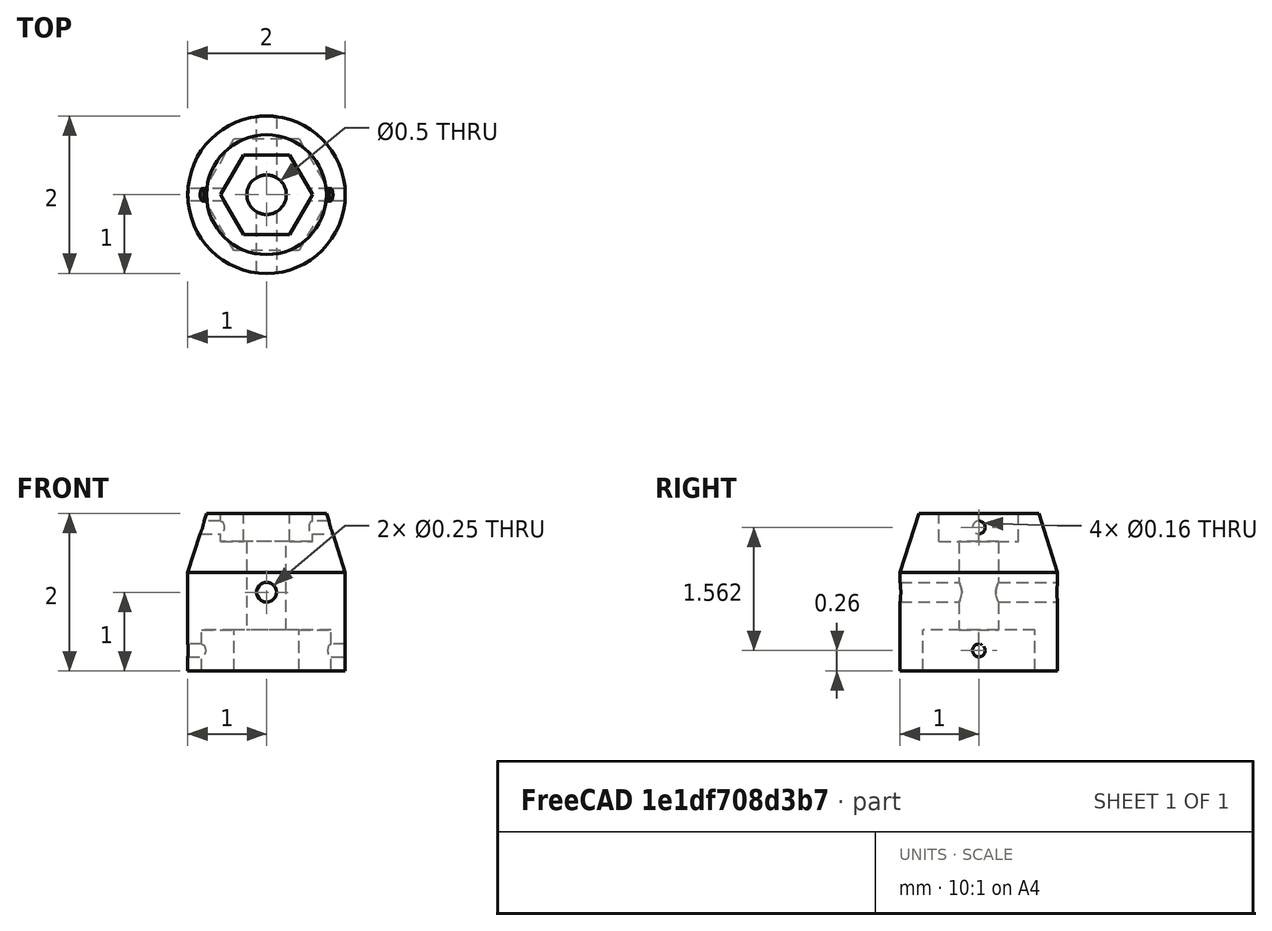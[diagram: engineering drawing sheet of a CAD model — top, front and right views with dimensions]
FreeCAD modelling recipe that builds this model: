
FCSTD DOCUMENT  (FreeCAD 0.20R29410 (Git))
Label: hex_dies
License: All rights reserved
LicenseURL: http://en.wikipedia.org/wiki/All_rights_reserved
objects: TechDraw::DrawViewDimension×11, Part::Cylinder×10, TechDraw::DrawViewBalloon×6, Part::Prism×4, TechDraw::DrawViewPart×4, TechDraw::DrawViewDimExtent×4, Part::Cone×2, Part::Fuse×2, Part::MultiFuse×2, Part::Cut×2, TechDraw::DrawSVGTemplate×2, TechDraw::DrawProjGroupItem×2, TechDraw::DrawViewSection×2, TechDraw::DrawPage×2, Spreadsheet::Sheet×2, TechDraw::DrawViewSpreadsheet×2, TechDraw::DrawProjGroup×1, TechDraw::DrawViewAnnotation×1
note: 22 computed .brp shape members not serialized (recipe doc carries the construction recipe); baked Part::Feature solids carry a one-line shape summary decoded from their .brp

FEATURE [Part::Cylinder] cylinder
  Angle = 360
  AttacherType = Attacher::AttachEngine3D
  FirstAngle = 0
  Height = 1.25
  Radius = 1
  SecondAngle = 0
FEATURE [Part::Cone] cylinder001
  Angle = 360
  AttacherType = Attacher::AttachEngine3D
  Height = 0.75
  Placement = pos=(0,0,1.25) rot=(0,0,1;0rad)
  Radius1 = 1
  Radius2 = 0.761
FEATURE [Part::Fuse] union
  Base = -> cylinder
  Tool = -> cylinder001
FEATURE [Part::Cylinder] cylinder002
  Angle = 360
  AttacherType = Attacher::AttachEngine3D
  FirstAngle = 0
  Height = 2.2
  Placement = pos=(0,0,-0.1) rot=(0,0,1;0rad)
  Radius = 0.2505
  SecondAngle = 0
FEATURE [Part::Prism] prism
  AttacherType = Attacher::AttachEngine3D
  Circumradius = 0.8225
  FirstAngle = 0
  Height = 0.62
  Placement = pos=(0,0,-0.1) rot=(0,0,1;0rad)
  Polygon = 6
  SecondAngle = 0
FEATURE [Part::Prism] prism001
  AttacherType = Attacher::AttachEngine3D
  Circumradius = 0.5835
  FirstAngle = 0
  Height = 0.455
  Placement = pos=(0,0,1.645) rot=(0,0,1;0rad)
  Polygon = 6
  SecondAngle = 0
FEATURE [Part::Cylinder] cylinder003
  Angle = 360
  AttacherType = Attacher::AttachEngine3D
  FirstAngle = 0
  Height = 2.2
  Placement = pos=(0,1.1,1) rot=(1,0,0;1.5708rad)
  Radius = 0.1255
  SecondAngle = 0
FEATURE [Part::Cylinder] cylinder004
  Angle = 360
  AttacherType = Attacher::AttachEngine3D
  FirstAngle = 0
  Height = 2.2
  Placement = pos=(-1.1,0,0.26) rot=(0,1,0;1.5708rad)
  Radius = 0.0805
  SecondAngle = 0
FEATURE [Part::Cylinder] cylinder005
  Angle = 360
  AttacherType = Attacher::AttachEngine3D
  FirstAngle = 0
  Height = 2.2
  Placement = pos=(-1.1,0,1.8225) rot=(0,1,0;1.5708rad)
  Radius = 0.0805
  SecondAngle = 0
FEATURE [Part::MultiFuse] union001
  Shapes = -> [cylinder002,prism,prism001,cylinder003,cylinder004,cylinder005]
FEATURE [Part::Cut] difference
  Base = -> union
  Tool = -> union001
FEATURE [TechDraw::DrawSVGTemplate] Template
  EditableTexts = Code=2022-10-20; CompanyAddress=<email> / Decatur, GA, US; CompanyName=Jason Antman; DrawingNumber=Rev. 1; DrawingTitle1=Hex Tailstock Die Holder; DrawingTitle2=github.com/<owner>/machining-projects; DrawingTitle3=Based on design by Quinn Dunki; DrawnBy=<owner>; Sheet=Sheet 1 of 2
  Height = 215.9
  Orientation = 1
  Width = 279.4
FEATURE [TechDraw::DrawProjGroupItem] ProjItem  label="Front"
  CoarseView = false
  Direction = (-0.707,0.5,0.5)
  Focus = 100
  HardHidden = false
  IsoCount = 0
  IsoHidden = false
  IsoVisible = true
  LockPosition = true
  Perspective = false
  Rotation = 0
  RotationVector = (0.5,0.854,-0.146)
  ScaleType = 2
  SeamHidden = false
  SeamVisible = true
  SmoothHidden = false
  SmoothVisible = true
  Source = -> [difference]
  Type = 0
  X = 0
  XDirection = (0.5,0.854,-0.146)
  Y = 0
FEATURE [TechDraw::DrawProjGroupItem] ProjItem001  label="Rear"
  CoarseView = false
  Direction = (0.707053,-0.500038,-0.500038)
  Focus = 100
  HardHidden = false
  IsoCount = 0
  IsoHidden = false
  IsoVisible = true
  LockPosition = false
  Perspective = false
  Rotation = 0
  RotationVector = (1,0,0)
  ScaleType = 2
  SeamHidden = false
  SeamVisible = true
  SmoothHidden = false
  SmoothVisible = true
  Source = -> [difference]
  Type = 3
  X = 69.0316
  XDirection = (-0.500196,-0.85348,0.146204)
  Y = 0
FEATURE [TechDraw::DrawProjGroup] ProjGroup
  Anchor = -> ProjItem
  AutoDistribute = true
  LockPosition = false
  ProjectionType = 0
  Rotation = 0
  Scale = 25
  ScaleType = 0
  Source = -> [difference]
  Views = -> [ProjItem,ProjItem001]
  X = 149.591
  Y = 154.677
  spacingX = 15
  spacingY = 15
FEATURE [TechDraw::DrawViewAnnotation] Annotation
  Font = osifont
  LineSpace = 80
  LockPosition = false
  MaxWidth = -1
  Rotation = 0
  ScaleType = 1
  Text = (1) Drill #20 & tap 10-24, 2 @ 180° apart | (2) Through-drill 1/4" and fit to rod | (3) Through-drill 1/2" and fit to rod
  TextSize = 5
  TextStyle = 0
  X = 206.892
  Y = 73.1604
FEATURE [TechDraw::DrawViewBalloon] Balloon
  BubbleShape = 0
  EndType = 0
  EndTypeScale = 1
  KinkLength = 5
  LockPosition = false
  OriginX = -0.52962
  OriginY = -0.399674
  Rotation = 0
  Scale = 25
  ScaleType = 0
  ShapeScale = 1
  SourceView = -> ProjItem
  Text = 1
  TextWrapLen = -1
  X = 0.284023
  Y = -0.281822
FEATURE [TechDraw::DrawViewBalloon] Balloon001
  BubbleShape = 0
  EndType = 0
  EndTypeScale = 1
  KinkLength = 5
  LockPosition = false
  OriginX = -0.405181
  OriginY = 1.02944
  Rotation = 0
  Scale = 25
  ScaleType = 0
  ShapeScale = 1
  SourceView = -> ProjItem
  Text = 1
  TextWrapLen = -1
  X = 0.367533
  Y = 0.874431
FEATURE [TechDraw::DrawViewBalloon] Balloon002
  BubbleShape = 0
  EndType = 0
  EndTypeScale = 1
  KinkLength = 5
  LockPosition = false
  OriginX = 0.731835
  OriginY = 0.0759214
  Rotation = 0
  Scale = 25
  ScaleType = 0
  ShapeScale = 1
  SourceView = -> ProjItem
  Text = 2
  TextWrapLen = -1
  X = -0.118965
  Y = 0.575776
FEATURE [TechDraw::DrawViewBalloon] Balloon003
  BubbleShape = 0
  EndType = 0
  EndTypeScale = 1
  KinkLength = 5
  LockPosition = false
  OriginX = 0.0291409
  OriginY = -0.722831
  Rotation = 0
  Scale = 25
  ScaleType = 0
  ShapeScale = 1
  SourceView = -> ProjItem
  Text = 3
  TextWrapLen = -1
  X = 1.02014
  Y = -1.25984
FEATURE [TechDraw::DrawViewPart] View
  CoarseView = false
  Direction = (1,0,0)
  Focus = 100
  HardHidden = false
  IsoCount = 0
  IsoHidden = false
  IsoVisible = true
  LockPosition = false
  Perspective = false
  Rotation = 0
  Scale = 25
  ScaleType = 0
  SeamHidden = false
  SeamVisible = true
  SmoothHidden = false
  SmoothVisible = true
  Source = -> [difference]
  X = 66.369
  XDirection = (0,1,0)
  Y = 165.933
FEATURE [TechDraw::DrawViewSection] SectionView
  BaseView = -> View
  CoarseView = false
  CutSurfaceDisplay = 2
  Direction = (0,1,0)
  FileGeomPattern = <path>
  FileHatchPattern = <path>
  Focus = 100
  FuseBeforeCut = false
  HardHidden = false
  HatchScale = 1
  IsoCount = 0
  IsoHidden = false
  IsoVisible = true
  LockPosition = false
  NameGeomPattern = Diamond
  Perspective = false
  Rotation = 0
  Scale = 25
  ScaleType = 0
  SeamHidden = false
  SeamVisible = true
  SectionDirection = 1
  SectionNormal = (0,1,0)
  SectionOrigin = (0,0,1)
  SmoothHidden = false
  SmoothVisible = true
  Source = -> [difference]
  X = 65.6869
  XDirection = (-1,0,0)
  Y = 155.018
FEATURE [TechDraw::DrawViewPart] View001
  CoarseView = false
  Direction = (0,-1,0)
  Focus = 100
  HardHidden = false
  IsoCount = 0
  IsoHidden = false
  IsoVisible = true
  LockPosition = false
  Perspective = false
  Rotation = 0
  Scale = 25
  ScaleType = 0
  SeamHidden = false
  SeamVisible = true
  SmoothHidden = false
  SmoothVisible = true
  Source = -> [difference]
  X = 56.819
  XDirection = (0,0,-1)
  Y = 85.4391
FEATURE [TechDraw::DrawViewSection] SectionView001
  BaseView = -> View001
  CoarseView = false
  CutSurfaceDisplay = 2
  Direction = (-1,0,0)
  FileGeomPattern = <path>
  FileHatchPattern = <path>
  Focus = 100
  FuseBeforeCut = false
  HardHidden = false
  HatchScale = 1
  IsoCount = 0
  IsoHidden = false
  IsoVisible = true
  LockPosition = false
  NameGeomPattern = Diamond
  Perspective = false
  Rotation = 0
  Scale = 25
  ScaleType = 0
  SeamHidden = false
  SeamVisible = true
  SectionDirection = 2
  SectionNormal = (-1,0,0)
  SectionOrigin = (0,0,1)
  SmoothHidden = false
  SmoothVisible = true
  Source = -> [difference]
  X = 67.3923
  XDirection = (0,0,-1)
  Y = 59.1764
FEATURE [TechDraw::DrawViewDimension] Dimension
  AngleOverride = false
  Arbitrary = false
  ArbitraryTolerances = false
  EqualTolerance = true
  ExtensionAngle = 0
  FormatSpec = %.3f
  FormatSpecOverTolerance = %+.3f
  FormatSpecUnderTolerance = %+.3f
  Inverted = false
  LineAngle = 0
  LockPosition = false
  MeasureType = 1
  OverTolerance = 0
  References2D = -> [SectionView]
  Rotation = 0
  Scale = 25
  ScaleType = 0
  TheoreticalExact = false
  Type = 1
  UnderTolerance = 0
  X = -0.682148
  Y = -4.04281
FEATURE [TechDraw::DrawViewDimExtent] DimExtent
  AngleOverride = false
  Arbitrary = false
  ArbitraryTolerances = false
  CosmeticTags = 4956244a-dadd-42d6-bc7f-95dd4a904bdd | ec660f67-53bf-4416-ad10-358074b2ad27
  DirExtent = 0
  EqualTolerance = true
  ExtensionAngle = 0
  FormatSpec = %.3f
  FormatSpecOverTolerance = %+.3f
  FormatSpecUnderTolerance = %+.3f
  Inverted = false
  LineAngle = 0
  LockPosition = false
  MeasureType = 1
  OverTolerance = 0
  References2D = -> [SectionView]
  Rotation = 0
  Scale = 25
  ScaleType = 0
  Source = -> [SectionView]
  TheoreticalExact = false
  Type = 1
  UnderTolerance = 0
  X = 0.682148
  Y = 36.1539
FEATURE [TechDraw::DrawViewDimExtent] DimExtent001
  AngleOverride = false
  Arbitrary = false
  ArbitraryTolerances = false
  CosmeticTags = 9ed5d077-f906-4c76-ad73-dbdbe7db25b5 | b98ef590-0970-4765-b477-5c79632b2bf6
  DirExtent = 0
  EqualTolerance = true
  ExtensionAngle = 0
  FormatSpec = %.3f
  FormatSpecOverTolerance = %+.3f
  FormatSpecUnderTolerance = %+.3f
  Inverted = false
  LineAngle = 0
  LockPosition = false
  MeasureType = 1
  OverTolerance = 0
  References2D = -> [SectionView]
  Rotation = 0
  Scale = 25
  ScaleType = 0
  Source = -> [SectionView]
  TheoreticalExact = false
  Type = 1
  UnderTolerance = 0
  X = -0.341074
  Y = -28.9913
FEATURE [TechDraw::DrawViewDimension] Dimension001
  AngleOverride = false
  Arbitrary = false
  ArbitraryTolerances = false
  EqualTolerance = true
  ExtensionAngle = 0
  FormatSpec = %.3f
  FormatSpecOverTolerance = %+.3f
  FormatSpecUnderTolerance = %+.3f
  Inverted = false
  LineAngle = 0
  LockPosition = false
  MeasureType = 1
  OverTolerance = 0
  References2D = -> [SectionView]
  Rotation = 0
  Scale = 25
  ScaleType = 0
  TheoreticalExact = false
  Type = 2
  UnderTolerance = 0
  X = 31.3614
  Y = 10.5616
FEATURE [TechDraw::DrawViewDimension] Dimension002
  AngleOverride = false
  Arbitrary = false
  ArbitraryTolerances = false
  EqualTolerance = true
  ExtensionAngle = 0
  FormatSpec = %.3f
  FormatSpecOverTolerance = %+.3f
  FormatSpecUnderTolerance = %+.3f
  Inverted = false
  LineAngle = 0
  LockPosition = false
  MeasureType = 1
  OverTolerance = 0
  References2D = -> [SectionView]
  Rotation = 0
  Scale = 25
  ScaleType = 0
  TheoreticalExact = false
  Type = 2
  UnderTolerance = 0
  X = 31.4279
  Y = -15.6589
FEATURE [TechDraw::DrawViewDimExtent] DimExtent002
  AngleOverride = false
  Arbitrary = false
  ArbitraryTolerances = false
  CosmeticTags = 1bfcef3d-2256-4522-bb0f-059edc9a38db | 6c0ead27-f160-403d-935c-1c1f8d771ce4
  DirExtent = 1
  EqualTolerance = true
  ExtensionAngle = 0
  FormatSpec = %.3f
  FormatSpecOverTolerance = %+.3f
  FormatSpecUnderTolerance = %+.3f
  Inverted = false
  LineAngle = 0
  LockPosition = false
  MeasureType = 1
  OverTolerance = 0
  References2D = -> [SectionView]
  Rotation = 0
  Scale = 25
  ScaleType = 0
  Source = -> [SectionView]
  TheoreticalExact = false
  Type = 2
  UnderTolerance = 0
  X = 40.2468
  Y = 1.70537
FEATURE [TechDraw::DrawViewDimension] Dimension005
  AngleOverride = false
  Arbitrary = false
  ArbitraryTolerances = false
  EqualTolerance = true
  ExtensionAngle = 0
  FormatSpec = %.3f
  FormatSpecOverTolerance = %+.3f
  FormatSpecUnderTolerance = %+.3f
  Inverted = false
  LineAngle = 0
  LockPosition = false
  MeasureType = 1
  OverTolerance = 0
  References2D = -> [SectionView001]
  Rotation = 0
  Scale = 25
  ScaleType = 0
  TheoreticalExact = false
  Type = 1
  UnderTolerance = 0
  X = 9.64577
  Y = 44.08
FEATURE [TechDraw::DrawViewDimension] Dimension006
  AngleOverride = false
  Arbitrary = false
  ArbitraryTolerances = false
  EqualTolerance = true
  ExtensionAngle = 0
  FormatSpec = %.3f
  FormatSpecOverTolerance = %+.3f
  FormatSpecUnderTolerance = %+.3f
  Inverted = false
  LineAngle = 0
  LockPosition = false
  MeasureType = 1
  OverTolerance = 0
  References2D = -> [SectionView001]
  Rotation = 0
  Scale = 25
  ScaleType = 0
  TheoreticalExact = false
  Type = 1
  UnderTolerance = 0
  X = -22.7812
  Y = 35.4349
FEATURE [TechDraw::DrawViewDimension] Dimension007
  AngleOverride = false
  Arbitrary = false
  ArbitraryTolerances = false
  EqualTolerance = true
  ExtensionAngle = 0
  FormatSpec = %.3f
  FormatSpecOverTolerance = %+.3f
  FormatSpecUnderTolerance = %+.3f
  Inverted = false
  LineAngle = 0
  LockPosition = false
  MeasureType = 1
  OverTolerance = 0
  References2D = -> [SectionView001]
  Rotation = 0
  Scale = 25
  ScaleType = 0
  TheoreticalExact = false
  Type = 1
  UnderTolerance = 0
  X = 15.658
  Y = 35.5301
FEATURE [TechDraw::DrawViewDimension] Dimension008
  AngleOverride = false
  Arbitrary = false
  ArbitraryTolerances = false
  EqualTolerance = true
  ExtensionAngle = 0
  FormatSpec = %.3f
  FormatSpecOverTolerance = %+.3f
  FormatSpecUnderTolerance = %+.3f
  Inverted = false
  LineAngle = 0
  LockPosition = false
  MeasureType = 1
  OverTolerance = 0
  References2D = -> [SectionView]
  Rotation = 0
  Scale = 25
  ScaleType = 0
  TheoreticalExact = false
  Type = 6
  UnderTolerance = 0
  X = -36.6373
  Y = 25.0755
FEATURE [TechDraw::DrawViewDimExtent] DimExtent003
  AngleOverride = false
  Arbitrary = false
  ArbitraryTolerances = false
  CosmeticTags = c99aefa7-8a50-471b-9c00-c3947b8e92fc | 33418c46-6f19-47d5-a466-5f668b27f0b3
  DirExtent = 1
  EqualTolerance = true
  ExtensionAngle = 0
  FormatSpec = %.3f
  FormatSpecOverTolerance = %+.3f
  FormatSpecUnderTolerance = %+.3f
  Inverted = false
  LineAngle = 0
  LockPosition = false
  MeasureType = 1
  OverTolerance = 0
  References2D = -> [SectionView]
  Rotation = 0
  Scale = 25
  ScaleType = 0
  Source = -> [SectionView]
  TheoreticalExact = false
  Type = 2
  UnderTolerance = 0
  X = -36.4949
  Y = -5.45719
FEATURE [TechDraw::DrawPage] Page  label="Page1"
  KeepUpdated = true
  NextBalloonIndex = 5
  ProjectionType = 0
  Scale = 25
  Template = -> Template
  Views = -> [ProjGroup,Annotation,Balloon,Balloon001,Balloon002,Balloon003,View,SectionView,View001,SectionView001,Dimension,DimExtent,DimExtent001,Dimension001,Dimension002,DimExtent002,Dimension005,Dimension006,Dimension007,Dimension008,DimExtent003]
FEATURE [TechDraw::DrawSVGTemplate] Template002
  EditableTexts = Code=2022-10-20; CompanyAddress=<email> / Decatur, GA, US; CompanyName=Jason Antman; DrawingNumber=Rev. 1; DrawingTitle1=Hex Tailstock Die Holder; DrawingTitle2=github.com/<owner>/machining-projects; DrawnBy=<owner>; Sheet=Sheet 2 of 2
  Height = 215.9
  Orientation = 1
  Width = 279.4
FEATURE [Part::Cylinder] cylinder006
  Angle = 360
  AttacherType = Attacher::AttachEngine3D
  FirstAngle = 0
  Height = 1.25
  Radius = 1
  SecondAngle = 0
FEATURE [Part::Cone] cylinder007
  Angle = 360
  AttacherType = Attacher::AttachEngine3D
  Height = 0.75
  Placement = pos=(0,0,1.25) rot=(0,0,1;0rad)
  Radius1 = 1
  Radius2 = 0.761
FEATURE [Part::Cylinder] cylinder008
  Angle = 360
  AttacherType = Attacher::AttachEngine3D
  FirstAngle = 0
  Height = 2.2
  Placement = pos=(0,0,-0.1) rot=(0,0,1;0rad)
  Radius = 0.2505
  SecondAngle = 0
FEATURE [Part::Cylinder] cylinder009
  Angle = 360
  AttacherType = Attacher::AttachEngine3D
  FirstAngle = 0
  Height = 2.2
  Placement = pos=(0,1.1,1) rot=(1,0,0;1.5708rad)
  Radius = 0.1255
  SecondAngle = 0
FEATURE [Part::Cylinder] cylinder010
  Angle = 360
  AttacherType = Attacher::AttachEngine3D
  FirstAngle = 0
  Height = 2.2
  Placement = pos=(-1.1,0,0.26) rot=(0,1,0;1.5708rad)
  Radius = 0.0805
  SecondAngle = 0
FEATURE [Part::Cylinder] cylinder011
  Angle = 360
  AttacherType = Attacher::AttachEngine3D
  FirstAngle = 0
  Height = 2.2
  Placement = pos=(-1.1,0,1.8225) rot=(0,1,0;1.5708rad)
  Radius = 0.0805
  SecondAngle = 0
FEATURE [Part::Prism] prism002
  AttacherType = Attacher::AttachEngine3D
  Circumradius = 0.8225
  FirstAngle = 0
  Height = 0.62
  Placement = pos=(0,0,-0.1) rot=(0,0,1;0rad)
  Polygon = 6
  SecondAngle = 0
FEATURE [Part::Prism] prism003
  AttacherType = Attacher::AttachEngine3D
  Circumradius = 0.5835
  FirstAngle = 0
  Height = 0.455
  Placement = pos=(0,0,1.645) rot=(0,0,1;0rad)
  Polygon = 6
  SecondAngle = 0
FEATURE [Part::Fuse] union002
  Base = -> cylinder006
  Tool = -> cylinder007
FEATURE [Part::MultiFuse] union003
  Shapes = -> [cylinder008,prism002,prism003,cylinder009,cylinder010,cylinder011]
FEATURE [Part::Cut] difference001
  Base = -> union002
  Tool = -> union003
FEATURE [TechDraw::DrawViewPart] View006
  CoarseView = false
  Direction = (0,0,-1)
  Focus = 100
  HardHidden = false
  IsoCount = 0
  IsoHidden = false
  IsoVisible = true
  LockPosition = false
  Perspective = false
  Rotation = 0
  Scale = 30
  ScaleType = 0
  SeamHidden = false
  SeamVisible = true
  SmoothHidden = false
  SmoothVisible = true
  Source = -> [difference]
  X = 192.908
  XDirection = (1,0,0)
  Y = 158.429
FEATURE [TechDraw::DrawViewPart] View007
  CoarseView = false
  Direction = (0,0,1)
  Focus = 100
  HardHidden = false
  IsoCount = 0
  IsoHidden = false
  IsoVisible = true
  LockPosition = false
  Perspective = false
  Rotation = 0
  Scale = 30
  ScaleType = 0
  SeamHidden = false
  SeamVisible = true
  SmoothHidden = false
  SmoothVisible = true
  Source = -> [difference]
  X = 74.8959
  XDirection = (-1,0,0)
  Y = 159.452
FEATURE [TechDraw::DrawViewDimension] Dimension013
  AngleOverride = false
  Arbitrary = false
  ArbitraryTolerances = false
  EqualTolerance = true
  ExtensionAngle = 0
  FormatSpec = %.3f
  FormatSpecOverTolerance = %+.3f
  FormatSpecUnderTolerance = %+.3f
  Inverted = false
  LineAngle = 0
  LockPosition = false
  MeasureType = 1
  OverTolerance = 0
  References2D = -> [View006]
  Rotation = 0
  Scale = 30
  ScaleType = 0
  TheoreticalExact = false
  Type = 0
  UnderTolerance = 0
  X = 11.226
  Y = 36.8372
FEATURE [TechDraw::DrawViewDimension] Dimension014
  AngleOverride = false
  Arbitrary = false
  ArbitraryTolerances = false
  EqualTolerance = true
  ExtensionAngle = 0
  FormatSpec = %.3f
  FormatSpecOverTolerance = %+.3f
  FormatSpecUnderTolerance = %+.3f
  Inverted = false
  LineAngle = 0
  LockPosition = false
  MeasureType = 1
  OverTolerance = 0
  References2D = -> [View007]
  Rotation = 0
  Scale = 30
  ScaleType = 0
  TheoreticalExact = false
  Type = 0
  UnderTolerance = 0
  X = 16.0882
  Y = 34.4847
FEATURE [TechDraw::DrawViewDimension] Dimension015
  AngleOverride = false
  Arbitrary = false
  ArbitraryTolerances = false
  EqualTolerance = true
  ExtensionAngle = 0
  FormatSpec = %.3f
  FormatSpecOverTolerance = %+.3f
  FormatSpecUnderTolerance = %+.3f
  Inverted = false
  LineAngle = 0
  LockPosition = false
  MeasureType = 1
  OverTolerance = 0
  References2D = -> [View006]
  Rotation = 0
  Scale = 30
  ScaleType = 0
  TheoreticalExact = false
  Type = 0
  UnderTolerance = 0
  X = -28.9913
  Y = 24.6698
FEATURE [TechDraw::DrawViewDimension] Dimension016
  AngleOverride = false
  Arbitrary = false
  ArbitraryTolerances = false
  EqualTolerance = true
  ExtensionAngle = 0
  FormatSpec = %.3f
  FormatSpecOverTolerance = %+.3f
  FormatSpecUnderTolerance = %+.3f
  Inverted = false
  LineAngle = 0
  LockPosition = false
  MeasureType = 1
  OverTolerance = 0
  References2D = -> [View007]
  Rotation = 0
  Scale = 30
  ScaleType = 0
  TheoreticalExact = false
  Type = 0
  UnderTolerance = 0
  X = -30.3556
  Y = 22.6234
FEATURE [Spreadsheet::Sheet] Spreadsheet  label="SmallHoles"
  cells = A1=Hole; B1=Angle; C1=X; D1=Y; A2=1; B2==0°; C2=0.5835; D2=0; A3=2; B3==60°; C3=0.2918; D3=0.5053; A4=3; B4==120°; C4=-0.2918; D4=0.5053; A5=4; B5==180°; C5=-0.5835; D5=0; A6=5; B6==240°; C6=-0.2918; D6=-0.5053; A7=6; B7==300°; C7=0.2918; D7=-0.5053
FEATURE [Spreadsheet::Sheet] Spreadsheet001  label="LargeHoles"
  cells = A1=Hole; B1=Angle; C1=X; D1=Y; A2=1; B2==0°; C2=0.8225; D2=0; A3=2; B3==60°; C3=0.4113; D3=0.7123; A4=3; B4==120°; C4=-0.4113; D4=0.7123; A5=4; B5==180°; C5=-0.8225; D5=0; A6=5; B6==240°; C6=-0.4113; D6=-0.7123; A7=6; B7==300°; C7=0.4113; D7=-0.7123
FEATURE [TechDraw::DrawViewSpreadsheet] Sheet
  CellEnd = D7
  CellStart = A1
  Font = osifont
  LineWidth = 0.35
  LockPosition = false
  Rotation = 0
  ScaleType = 2
  Source = -> Spreadsheet
  Symbol = <blob: 5986 chars omitted>
  TextSize = 12
  X = 76.2602
  Y = 92.6017
FEATURE [TechDraw::DrawViewSpreadsheet] Sheet001
  CellEnd = D7
  CellStart = A1
  Font = osifont
  LineWidth = 0.35
  LockPosition = false
  Rotation = 0
  ScaleType = 2
  Source = -> Spreadsheet001
  Symbol = <blob: 6001 chars omitted>
  TextSize = 12
  X = 196.318
  Y = 91.9195
FEATURE [TechDraw::DrawViewBalloon] Balloon004
  BubbleShape = 5
  EndType = 0
  EndTypeScale = 1
  KinkLength = 5
  LockPosition = false
  OriginX = 0
  OriginY = 0
  Rotation = 0
  Scale = 30
  ScaleType = 0
  ShapeScale = 1
  SourceView = -> View006
  Text = 0,0
  TextWrapLen = -1
  X = 1.2806
  Y = -0.629415
FEATURE [TechDraw::DrawViewBalloon] Balloon005
  BubbleShape = 5
  EndType = 0
  EndTypeScale = 1
  KinkLength = 5
  LockPosition = false
  OriginX = 0
  OriginY = 0
  Rotation = 0
  Scale = 30
  ScaleType = 0
  ShapeScale = 1
  SourceView = -> View007
  Text = 0,0
  TextWrapLen = -1
  X = 1.31471
  Y = -0.595308
FEATURE [TechDraw::DrawPage] Page002
  KeepUpdated = true
  NextBalloonIndex = 3
  ProjectionType = 0
  Scale = 30
  Template = -> Template002
  Views = -> [View006,View007,Dimension013,Dimension014,Dimension015,Dimension016,Sheet,Sheet001,Balloon004,Balloon005]
note: 4 file-system paths scrubbed to <path> (originals preserved in the JSON sidecar)
